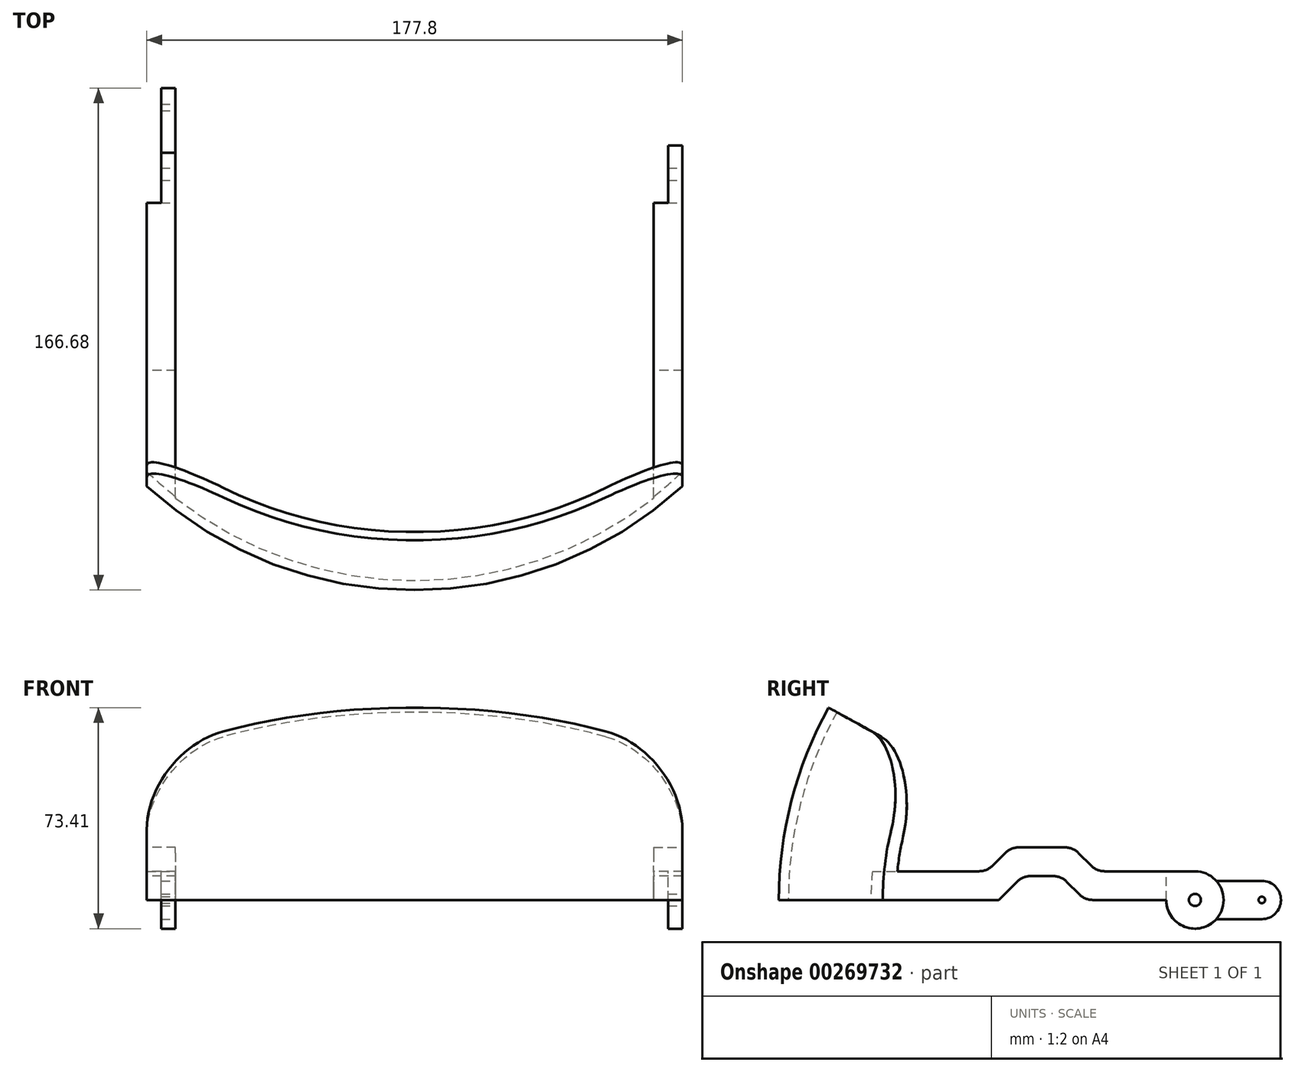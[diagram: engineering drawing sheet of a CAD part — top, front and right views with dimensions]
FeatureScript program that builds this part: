
annotation { "Feature Type Name" : "Feature", "Feature Type Description" : "" }
export const myFeature = defineFeature(function(context is Context, id is Id, definition is map)
    precondition{}
    {
        {
            var Q0;
            Q0=qCreatedBy(makeId("Right.planeOp"),FACE);
            var sketch = newSketch(context, id + "F0", { "sketchPlane" : qUnion([Q0])});
            skArc(sketch, "E0", {"start": v(0, 131.76) * mm, "mid": v(-131.76, 0) * mm, "end": v(0, -131.76) * mm});
            skArc(sketch, "E1", {"start": v(0, 128.59) * mm, "mid": v(-128.59, 0) * mm, "end": v(0, -128.59) * mm});
            skLineSegment(sketch, "E2", {"start": v(0, 131.76) * mm, "end": v(0, 128.59) * mm});
            skLineSegment(sketch, "E3.trimOffspring", {"start": v(0, 0) * mm, "end": v(0, -131.76) * mm});
            skPoint(sketch, "E4.orphan", {"position": v(0, 135.47) * mm});
            skSolve(sketch);
        }
        {
            var Q0;
            Q0=qSketchRegion(id+"F0",true);
            var Q1;
            Q1=sQuery(id+"F0.wireOp",EDGE,"E3.trimOffspring");
            revolve(context, id + "F1", {"entities" : qUnion([Q0]), "axis" : qUnion([Q1]), "revolveType" : RevolveType.FULL});
        }
        {
            var Q0;
            Q0=qCreatedBy(makeId("Front.planeOp"),FACE);
            var sketch = newSketch(context, id + "F2", { "sketchPlane" : qUnion([Q0])});
            skLineSegment(sketch, "E5.left", {"start": v(88.9, 152.6) * mm, "end": v(88.9, -152.6) * mm});
            skLineSegment(sketch, "E5.right", {"start": v(-88.9, 152.6) * mm, "end": v(-88.9, -152.6) * mm});
            skPoint(sketch, "E5.middle", {"position": v(0, 0) * mm});
            skLineSegment(sketch, "E6.bottom", {"start": v(230.94, 152.6) * mm, "end": v(88.9, 152.6) * mm});
            skLineSegment(sketch, "E6.top", {"start": v(230.94, -152.6) * mm, "end": v(88.9, -152.6) * mm});
            skLineSegment(sketch, "E6.left", {"start": v(230.94, 152.6) * mm, "end": v(230.94, -152.6) * mm});
            skLineSegment(sketch, "E6.right", {"start": v(-230.94, 152.6) * mm, "end": v(-230.94, -152.6) * mm});
            skLineSegment(sketch, "E7.trimOffspring", {"start": v(-88.9, 152.6) * mm, "end": v(-230.94, 152.6) * mm});
            skPoint(sketch, "E5.bottom.start.orphan", {"position": v(88.9, 254.33) * mm});
            skPoint(sketch, "E8.orphan", {"position": v(-88.9, 254.33) * mm});
            skLineSegment(sketch, "E9.trimOffspring", {"start": v(-88.9, -152.6) * mm, "end": v(-230.94, -152.6) * mm});
            skPoint(sketch, "E5.top.end.orphan", {"position": v(-88.9, -254.33) * mm});
            skPoint(sketch, "E5.top.start.orphan", {"position": v(88.9, -254.33) * mm});
            skSolve(sketch);
        }
        {
            var Q0;
            Q0=qSketchRegion(id+"F2",true);
            extrude(context, id + "F3", {"entities" : qUnion([Q0]), "operationType" : NewBodyOperationType.REMOVE, "endBound" : BoundingType.SYMMETRIC, "oppositeDirection" : true, "depth" : 304.8 * mm});
        }
        {
            var Q0;
            Q0=qCreatedBy(makeId("Right.planeOp"),FACE);
            var sketch = newSketch(context, id + "F4", { "sketchPlane" : qUnion([Q0])});
            skLineSegment(sketch, "E10", {"start": v(0, 0) * mm, "end": v(-147.9, 0) * mm});
            skLineSegment(sketch, "E11", {"start": v(0, 0) * mm, "end": v(-129.35, 71.7) * mm});
            skArc(sketch, "E12", {"start": v(-147.9, 0) * mm, "mid": v(143.19, -37.03) * mm, "end": v(-129.35, 71.7) * mm});
            skSolve(sketch);
        }
        {
            var Q0;
            Q0=qSketchRegion(id+"F4",true);
            extrude(context, id + "F5", {"entities" : qUnion([Q0]), "operationType" : NewBodyOperationType.REMOVE, "endBound" : BoundingType.SYMMETRIC, "depth" : 304.8 * mm});
        }
        {
            var Q0;
            Q0=makeQuery(id+"F5.boolean.opBoolean","INTERSECT",EDGE,{"derivedFrom":[makeQuery(id+"F3.boolean.opBoolean","COPY",FACE,{"derivedFrom":makeQuery(id+"F3.opExtrude","SWEPT_FACE",FACE,{"disambiguationData":[OSD([sQuery(id+"F2.wireOp",EDGE,"E5.left")])]})}),makeQuery(id+"F5.opExtrude","SWEPT_FACE",FACE,{"disambiguationData":[OSD([sQuery(id+"F4.wireOp",EDGE,"E11")])]})]});
            var Q1;
            Q1=makeQuery(id+"F5.boolean.opBoolean","INTERSECT",EDGE,{"derivedFrom":[makeQuery(id+"F3.boolean.opBoolean","COPY",FACE,{"derivedFrom":makeQuery(id+"F3.opExtrude","SWEPT_FACE",FACE,{"disambiguationData":[OSD([sQuery(id+"F2.wireOp",EDGE,"E5.right")])]})}),makeQuery(id+"F5.opExtrude","SWEPT_FACE",FACE,{"disambiguationData":[OSD([sQuery(id+"F4.wireOp",EDGE,"E11")])]})]});
            fillet(context, id + "F6", {"entities" : qUnion([Q0, Q1]), "radius" : 25.4 * mm, "tangentPropagation" : true, "allowEdgeOverflow" : false});
        }
        {
            var Q0;
            Q0=qCreatedBy(makeId("Front.planeOp"),FACE);
            var sketch = newSketch(context, id + "F7", { "sketchPlane" : qUnion([Q0])});
            skLineSegment(sketch, "E13", {"start": v(88.9, 0) * mm, "end": v(79.38, 0) * mm});
            skLineSegment(sketch, "E14", {"start": v(88.9, 0) * mm, "end": v(88.9, 9.52) * mm});
            skLineSegment(sketch, "E15", {"start": v(-88.9, 0) * mm, "end": v(-88.9, 9.52) * mm});
            skLineSegment(sketch, "E16", {"start": v(88.9, 9.52) * mm, "end": v(79.38, 9.52) * mm});
            skLineSegment(sketch, "E17", {"start": v(79.38, 9.52) * mm, "end": v(79.38, 0) * mm});
            skLineSegment(sketch, "E18", {"start": v(-79.38, 9.52) * mm, "end": v(-79.38, 0) * mm});
            skLineSegment(sketch, "E19.trimOffspring", {"start": v(-79.38, 9.52) * mm, "end": v(-88.9, 9.52) * mm});
            skLineSegment(sketch, "E20.trimOffspring", {"start": v(-79.38, 0) * mm, "end": v(-88.9, 0) * mm});
            skPoint(sketch, "E21.orphan", {"position": v(-88.9, 10) * mm});
            skPoint(sketch, "E22.orphan", {"position": v(94.46, 0) * mm});
            skSolve(sketch);
        }
        {
            var Q0;
            Q0=qSketchRegion(id+"F7",true);
            var Q1;
            Q1=makeQuery(id+"F1.opRevolve","SWEPT_FACE",FACE,{"disambiguationData":[OSD([sQuery(id+"F0.wireOp",EDGE,"E1")])]});
            extrude(context, id + "F8", {"entities" : qUnion([Q0]), "operationType" : NewBodyOperationType.ADD, "endBound" : BoundingType.UP_TO_SURFACE, "endBoundEntityFace" : qUnion([Q1]), "depth" : 25.4 * mm});
        }
        {
            var Q0;
            Q0=makeQuery(id+"F8.opExtrude","CAP_FACE",FACE,{"disambiguationData":[OSD([sQuery(id+"F7.wireOp",EDGE,"E13"),sQuery(id+"F7.wireOp",EDGE,"E14"),sQuery(id+"F7.wireOp",EDGE,"E16"),sQuery(id+"F7.wireOp",EDGE,"E17")])],"isStart":true});
            var sketch = newSketch(context, id + "F9", { "sketchPlane" : qUnion([Q0])});
            skLineSegment(sketch, "E23.bottom", {"start": v(-88.9, 9.52) * mm, "end": v(-79.38, 9.52) * mm});
            skLineSegment(sketch, "E23.top", {"start": v(-88.9, 0) * mm, "end": v(-79.38, 0) * mm});
            skLineSegment(sketch, "E23.left", {"start": v(-88.9, 9.52) * mm, "end": v(-88.9, 0) * mm});
            skLineSegment(sketch, "E23.right", {"start": v(-79.38, 9.52) * mm, "end": v(-79.38, 0) * mm});
            skSolve(sketch);
        }
        {
            var Q0;
            Q0=makeQuery(id+"F8.opExtrude","CAP_FACE",FACE,{"disambiguationData":[OSD([sQuery(id+"F7.wireOp",EDGE,"E15"),sQuery(id+"F7.wireOp",EDGE,"E18"),sQuery(id+"F7.wireOp",EDGE,"E19.trimOffspring"),sQuery(id+"F7.wireOp",EDGE,"E20.trimOffspring")])],"isStart":true});
            var sketch = newSketch(context, id + "F10", { "sketchPlane" : qUnion([Q0])});
            skLineSegment(sketch, "E24.bottom", {"start": v(79.38, 9.52) * mm, "end": v(88.9, 9.52) * mm});
            skLineSegment(sketch, "E24.top", {"start": v(79.38, 0) * mm, "end": v(88.9, 0) * mm});
            skLineSegment(sketch, "E24.left", {"start": v(79.38, 9.52) * mm, "end": v(79.38, 0) * mm});
            skLineSegment(sketch, "E24.right", {"start": v(88.9, 9.52) * mm, "end": v(88.9, 0) * mm});
            skSolve(sketch);
        }
        {
            var Q0;
            Q0 = qSketchRegion(id + "F9", true);
            var Q1;
            Q1 = qSketchRegion(id + "F10", true);
            extrude(context, id + "F11", {"entities" : qUnion([Q0, Q1]), "operationType" : NewBodyOperationType.ADD, "depth" : 6.35 * mm, "offsetDistance" : 25.4 * mm});
        }
        {
            var Q0;
            Q0=makeQuery(id+"F8.boolean.opBoolean","MERGE",FACE,{"derivedFrom":[makeQuery(id+"F3.boolean.opBoolean","COPY",FACE,{"derivedFrom":makeQuery(id+"F3.opExtrude","SWEPT_FACE",FACE,{"disambiguationData":[OSD([sQuery(id+"F2.wireOp",EDGE,"E5.left")])]})}),makeQuery(id+"F8.opExtrude","SWEPT_FACE",FACE,{"disambiguationData":[OSD([sQuery(id+"F7.wireOp",EDGE,"E14")])]})]});
            var sketch = newSketch(context, id + "F12", { "sketchPlane" : qUnion([Q0])});
            skLineSegment(sketch, "E25", {"start": v(-16.7, 0) * mm, "end": v(-30.16, 0) * mm});
            skPoint(sketch, "E26.endSnap0", {"position": v(6.35, 4.76) * mm});
            skLineSegment(sketch, "E27", {"start": v(-34.15, 17.46) * mm, "end": v(-54.75, 17.46) * mm});
            skLineSegment(sketch, "E28", {"start": v(-34.93, 17.46) * mm, "end": v(-34.93, 4.76) * mm});
            skLineSegment(sketch, "E29", {"start": v(-53.98, 17.46) * mm, "end": v(-53.98, 4.76) * mm});
            skLineSegment(sketch, "E30", {"start": v(-64.27, 7.94) * mm, "end": v(-24.63, 7.94) * mm});
            skPoint(sketch, "E31.orphan", {"position": v(-81.5, 4.76) * mm});
            skLineSegment(sketch, "E32", {"start": v(-53.98, 4.76) * mm, "end": v(-50.8, 7.94) * mm});
            skLineSegment(sketch, "E33", {"start": v(-34.93, 4.76) * mm, "end": v(-38.1, 7.94) * mm});
            skLineSegment(sketch, "E34", {"start": v(-53.98, 4.76) * mm, "end": v(-58.74, 0) * mm});
            skLineSegment(sketch, "E35", {"start": v(-34.93, 4.76) * mm, "end": v(-30.16, 0) * mm});
            skPoint(sketch, "E36.start.orphan", {"position": v(6.35, 19.8) * mm});
            skLineSegment(sketch, "E37", {"start": v(-54.75, 17.46) * mm, "end": v(-72.2, 0) * mm});
            skLineSegment(sketch, "E38", {"start": v(-34.15, 17.46) * mm, "end": v(-16.7, 0) * mm});
            skPoint(sketch, "E39.orphan", {"position": v(6.35, 17.46) * mm});
            skLineSegment(sketch, "E40.trimOffspring", {"start": v(-58.74, 0) * mm, "end": v(-72.2, 0) * mm});
            skSolve(sketch);
        }
        {
            var Q0;
            Q0=qSketchRegion(id+"F12",true);
            extrude(context, id + "F13", {"entities" : qUnion([Q0]), "operationType" : NewBodyOperationType.ADD, "oppositeDirection" : true, "depth" : 9.52 * mm});
        }
        {
            var Q0;
            Q0=makeQuery(id+"F8.boolean.opBoolean","MERGE",FACE,{"derivedFrom":[makeQuery(id+"F3.boolean.opBoolean","COPY",FACE,{"derivedFrom":makeQuery(id+"F3.opExtrude","SWEPT_FACE",FACE,{"disambiguationData":[OSD([sQuery(id+"F2.wireOp",EDGE,"E5.right")])]})}),makeQuery(id+"F8.opExtrude","SWEPT_FACE",FACE,{"disambiguationData":[OSD([sQuery(id+"F7.wireOp",EDGE,"E15")])]})]});
            var sketch = newSketch(context, id + "F14", { "sketchPlane" : qUnion([Q0])});
            skLineSegment(sketch, "E41", {"start": v(34.15, 17.46) * mm, "end": v(54.75, 17.46) * mm});
            skLineSegment(sketch, "E42", {"start": v(34.93, 7.94) * mm, "end": v(34.93, 0) * mm});
            skLineSegment(sketch, "E43", {"start": v(53.98, 7.94) * mm, "end": v(53.98, 0) * mm});
            skLineSegment(sketch, "E44", {"start": v(34.93, 0) * mm, "end": v(53.98, 0) * mm});
            skLineSegment(sketch, "E45", {"start": v(34.93, 4.76) * mm, "end": v(38.1, 7.94) * mm});
            skLineSegment(sketch, "E46", {"start": v(53.98, 4.76) * mm, "end": v(49.21, 9.53) * mm});
            skLineSegment(sketch, "E47", {"start": v(24.63, 7.94) * mm, "end": v(34.93, 7.94) * mm});
            skLineSegment(sketch, "E48", {"start": v(34.15, 17.46) * mm, "end": v(24.63, 7.94) * mm});
            skLineSegment(sketch, "E49", {"start": v(54.75, 17.46) * mm, "end": v(64.27, 7.94) * mm});
            skPoint(sketch, "E50.orphan", {"position": v(34.93, 9.52) * mm});
            skLineSegment(sketch, "E51.trimOffspring", {"start": v(53.98, 7.94) * mm, "end": v(64.27, 7.94) * mm});
            skPoint(sketch, "E52.orphan", {"position": v(53.98, 9.52) * mm});
            skSolve(sketch);
        }
        {
            var Q0;
            Q0=qSketchRegion(id+"F14",true);
            extrude(context, id + "F15", {"entities" : qUnion([Q0]), "operationType" : NewBodyOperationType.ADD, "oppositeDirection" : true, "depth" : 9.52 * mm});
        }
        {
            var Q0;
            Q0=qCreatedBy(makeId("Right.planeOp"),FACE);
            var sketch = newSketch(context, id + "F16", { "sketchPlane" : qUnion([Q0])});
            skLineSegment(sketch, "E53", {"start": v(-30.16, 0) * mm, "end": v(-58.74, 0) * mm});
            skLineSegment(sketch, "E54", {"start": v(-38.1, 7.94) * mm, "end": v(-50.8, 7.94) * mm});
            skLineSegment(sketch, "E55", {"start": v(-53.98, 7.94) * mm, "end": v(-53.98, 4.76) * mm});
            skLineSegment(sketch, "E56.trimOffspring", {"start": v(-34.93, 4.76) * mm, "end": v(-34.93, 7.94) * mm});
            skLineSegment(sketch, "E57", {"start": v(-53.98, 4.76) * mm, "end": v(-50.8, 7.94) * mm});
            skLineSegment(sketch, "E58", {"start": v(-34.93, 4.76) * mm, "end": v(-38.1, 7.94) * mm});
            skLineSegment(sketch, "E59", {"start": v(-53.98, 4.76) * mm, "end": v(-58.74, 0) * mm});
            skLineSegment(sketch, "E60", {"start": v(-34.93, 4.76) * mm, "end": v(-30.16, 0) * mm});
            skSolve(sketch);
        }
        {
            var Q0;
            Q0=qSketchRegion(id+"F16",true);
            extrude(context, id + "F17", {"entities" : qUnion([Q0]), "operationType" : NewBodyOperationType.REMOVE, "endBound" : BoundingType.SYMMETRIC, "depth" : 177.8 * mm});
        }
        {
            var Q0;
            Q0=makeQuery(id+"F9Fqv3LpDGS5zFg_1.boolean.opBoolean","MERGE",FACE,{"derivedFrom":[makeQuery(id+"F8.boolean.opBoolean","MERGE",FACE,{"derivedFrom":[makeQuery(id+"F3.boolean.opBoolean","COPY",FACE,{"derivedFrom":makeQuery(id+"F3.opExtrude","SWEPT_FACE",FACE,{"disambiguationData":[OSD([sQuery(id+"F2.wireOp",EDGE,"E5.left")])]})}),makeQuery(id+"F8.opExtrude","SWEPT_FACE",FACE,{"disambiguationData":[OSD([sQuery(id+"F7.wireOp",EDGE,"E14")])]})]}),makeQuery(id+"F9Fqv3LpDGS5zFg_1.opExtrude","CAP_FACE",FACE,{"disambiguationData":[OSD([sQuery(id+"Fdyxyt73cwK6mQ5_1.wireOp",EDGE,"uge7HxcK-xsYJ-EXUT-pD71-h3y1mwA4NyrV"),sQuery(id+"Fdyxyt73cwK6mQ5_1.wireOp",EDGE,"hfxr85zl-CjJz-dNnQ-cUyG-KzP6Vcheir9o"),sQuery(id+"Fdyxyt73cwK6mQ5_1.wireOp",EDGE,"DYdveK2D-yC2o-hGCK-GH33-UXKGGb30pmTF"),sQuery(id+"Fdyxyt73cwK6mQ5_1.wireOp",EDGE,"KyHsQCAR-jBkV-1PyX-yX3m-mguW6c5BXjM3"),sQuery(id+"Fdyxyt73cwK6mQ5_1.wireOp",EDGE,"KXiKUkZQ-NJSx-R7BF-pjD5-MABOeaKY5b3t"),sQuery(id+"Fdyxyt73cwK6mQ5_1.wireOp",EDGE,"uAoFoTMZ-oCW3-4zug-ka1U-f82iXX2Ucrwf"),sQuery(id+"Fdyxyt73cwK6mQ5_1.wireOp",EDGE,"oFfLLbmo-RIOd-E5QO-eRZp-mn8jqRh1hiLr"),sQuery(id+"Fdyxyt73cwK6mQ5_1.wireOp",EDGE,"XboE2R6W-MqqC-2Aew-ZZfI-9xdbT96ioL7k"),sQuery(id+"Fdyxyt73cwK6mQ5_1.wireOp",EDGE,"il7hj7Cw-iAn3-ZAEo-7ila-wyK5fjaZt0oG"),sQuery(id+"Fdyxyt73cwK6mQ5_1.wireOp",EDGE,"2c3155a9-a74c-4d56-af0e-1345a1cb9d5a.trimOffspring")])],"isStart":true})]});
            var sketch = newSketch(context, id + "F18", { "sketchPlane" : qUnion([Q0])});
            skCircle(sketch, "E61", {"center": v(6.35, 0) * mm, "radius": 9.52 * mm});
            skSolve(sketch);
        }
        {
            var Q0;
            Q0=qSketchRegion(id+"F18",true);
            extrude(context, id + "F19", {"entities" : qUnion([Q0]), "operationType" : NewBodyOperationType.ADD, "oppositeDirection" : true, "depth" : 4.76 * mm});
        }
        {
            var Q0;
            Q0=makeQuery(id+"F15.boolean.opBoolean","MERGE",FACE,{"derivedFrom":[makeQuery(id+"F8.opExtrude","SWEPT_FACE",FACE,{"disambiguationData":[OSD([sQuery(id+"F7.wireOp",EDGE,"E18")])]}),makeQuery(id+"F15.opExtrude","CAP_FACE",FACE,{"disambiguationData":[OSD([sQuery(id+"F14.wireOp",EDGE,"E41"),sQuery(id+"F14.wireOp",EDGE,"E42"),sQuery(id+"F14.wireOp",EDGE,"E43"),sQuery(id+"F14.wireOp",EDGE,"E44"),sQuery(id+"F14.wireOp",EDGE,"E47"),sQuery(id+"F14.wireOp",EDGE,"E48"),sQuery(id+"F14.wireOp",EDGE,"E49"),sQuery(id+"F14.wireOp",EDGE,"E51.trimOffspring")])],"isStart":false})]});
            var sketch = newSketch(context, id + "F20", { "sketchPlane" : qUnion([Q0])});
            skCircle(sketch, "E62", {"center": v(6.35, 0) * mm, "radius": 9.52 * mm});
            skSolve(sketch);
        }
        {
            var Q0;
            Q0=qSketchRegion(id+"F20",true);
            extrude(context, id + "F21", {"entities" : qUnion([Q0]), "operationType" : NewBodyOperationType.ADD, "oppositeDirection" : true, "depth" : 4.76 * mm});
        }
        {
            var Q0;
            Q0=qCreatedBy(makeId("Right.planeOp"),FACE);
            var sketch = newSketch(context, id + "F22", { "sketchPlane" : qUnion([Q0])});
            skCircle(sketch, "E63", {"center": v(6.35, 0) * mm, "radius": 2 * mm});
            skSolve(sketch);
        }
        {
            var Q0;
            Q0=qSketchRegion(id+"F22",true);
            extrude(context, id + "F23", {"entities" : qUnion([Q0]), "operationType" : NewBodyOperationType.REMOVE, "endBound" : BoundingType.SYMMETRIC, "oppositeDirection" : true, "depth" : 177.8 * mm});
        }
        {
            var Q0;
            Q0=makeQuery(id+"F15.boolean.opBoolean","MERGE",FACE,{"derivedFrom":[makeQuery(id+"F8.boolean.opBoolean","MERGE",FACE,{"derivedFrom":[makeQuery(id+"F3.boolean.opBoolean","COPY",FACE,{"derivedFrom":makeQuery(id+"F3.opExtrude","SWEPT_FACE",FACE,{"disambiguationData":[OSD([sQuery(id+"F2.wireOp",EDGE,"E5.right")])]})}),makeQuery(id+"F8.opExtrude","SWEPT_FACE",FACE,{"disambiguationData":[OSD([sQuery(id+"F7.wireOp",EDGE,"E15")])]})]}),makeQuery(id+"F15.opExtrude","CAP_FACE",FACE,{"disambiguationData":[OSD([sQuery(id+"F14.wireOp",EDGE,"E41"),sQuery(id+"F14.wireOp",EDGE,"E42"),sQuery(id+"F14.wireOp",EDGE,"E43"),sQuery(id+"F14.wireOp",EDGE,"E44"),sQuery(id+"F14.wireOp",EDGE,"E47"),sQuery(id+"F14.wireOp",EDGE,"E48"),sQuery(id+"F14.wireOp",EDGE,"E49"),sQuery(id+"F14.wireOp",EDGE,"E51.trimOffspring")])],"isStart":true})]});
            var sketch = newSketch(context, id + "F24", { "sketchPlane" : qUnion([Q0])});
            skArc(sketch, "E64", {"start": v(-6.35, 9.52) * mm, "mid": v(-13.09, -6.74) * mm, "end": v(3.17, 0) * mm});
            skLineSegment(sketch, "E65", {"start": v(3.17, 0) * mm, "end": v(3.17, 9.52) * mm});
            skLineSegment(sketch, "E66", {"start": v(3.17, 9.52) * mm, "end": v(-6.35, 9.52) * mm});
            skSolve(sketch);
        }
        {
            var Q0;
            Q0=qSketchRegion(id+"F24",true);
            extrude(context, id + "F25", {"entities" : qUnion([Q0]), "operationType" : NewBodyOperationType.REMOVE, "oppositeDirection" : true, "depth" : 4.76 * mm});
        }
        {
            var Q0;
            Q0=makeQuery(id+"F9Fqv3LpDGS5zFg_1.boolean.opBoolean","MERGE",FACE,{"derivedFrom":[makeQuery(id+"F8.opExtrude","SWEPT_FACE",FACE,{"disambiguationData":[OSD([sQuery(id+"F7.wireOp",EDGE,"E17")])]}),makeQuery(id+"F9Fqv3LpDGS5zFg_1.opExtrude","CAP_FACE",FACE,{"disambiguationData":[OSD([sQuery(id+"Fdyxyt73cwK6mQ5_1.wireOp",EDGE,"uge7HxcK-xsYJ-EXUT-pD71-h3y1mwA4NyrV"),sQuery(id+"Fdyxyt73cwK6mQ5_1.wireOp",EDGE,"hfxr85zl-CjJz-dNnQ-cUyG-KzP6Vcheir9o"),sQuery(id+"Fdyxyt73cwK6mQ5_1.wireOp",EDGE,"DYdveK2D-yC2o-hGCK-GH33-UXKGGb30pmTF"),sQuery(id+"Fdyxyt73cwK6mQ5_1.wireOp",EDGE,"KyHsQCAR-jBkV-1PyX-yX3m-mguW6c5BXjM3"),sQuery(id+"Fdyxyt73cwK6mQ5_1.wireOp",EDGE,"KXiKUkZQ-NJSx-R7BF-pjD5-MABOeaKY5b3t"),sQuery(id+"Fdyxyt73cwK6mQ5_1.wireOp",EDGE,"uAoFoTMZ-oCW3-4zug-ka1U-f82iXX2Ucrwf"),sQuery(id+"Fdyxyt73cwK6mQ5_1.wireOp",EDGE,"oFfLLbmo-RIOd-E5QO-eRZp-mn8jqRh1hiLr"),sQuery(id+"Fdyxyt73cwK6mQ5_1.wireOp",EDGE,"XboE2R6W-MqqC-2Aew-ZZfI-9xdbT96ioL7k"),sQuery(id+"Fdyxyt73cwK6mQ5_1.wireOp",EDGE,"il7hj7Cw-iAn3-ZAEo-7ila-wyK5fjaZt0oG"),sQuery(id+"Fdyxyt73cwK6mQ5_1.wireOp",EDGE,"2c3155a9-a74c-4d56-af0e-1345a1cb9d5a.trimOffspring")])],"isStart":false})]});
            var sketch = newSketch(context, id + "F26", { "sketchPlane" : qUnion([Q0])});
            skArc(sketch, "E67", {"start": v(-6.35, 9.52) * mm, "mid": v(-13.09, -6.74) * mm, "end": v(3.17, 0) * mm});
            skLineSegment(sketch, "E68", {"start": v(3.17, 0) * mm, "end": v(3.17, 9.52) * mm});
            skLineSegment(sketch, "E69", {"start": v(3.17, 9.52) * mm, "end": v(-6.35, 9.52) * mm});
            skSolve(sketch);
        }
        {
            var Q0;
            Q0=qSketchRegion(id+"F26",true);
            extrude(context, id + "F27", {"entities" : qUnion([Q0]), "operationType" : NewBodyOperationType.REMOVE, "oppositeDirection" : true, "depth" : 4.76 * mm});
        }
        {
            var Q0;
            Q0=makeQuery(id+"F8.opExtrude","TWEAK_EDGE",EDGE,{"derivedFrom":[makeQuery(id+"F1.opRevolve","SWEPT_FACE",FACE,{"disambiguationData":[OSD([sQuery(id+"F0.wireOp",EDGE,"E1")])]}),makeQuery(id+"F7.imprint","IMPRINT",EDGE,{"derivedFrom":sQuery(id+"F7.wireOp",EDGE,"E19.trimOffspring")})]});
            var Q1;
            Q1=makeQuery(id+"F8.opExtrude","TWEAK_EDGE",EDGE,{"derivedFrom":[makeQuery(id+"F1.opRevolve","SWEPT_FACE",FACE,{"disambiguationData":[OSD([sQuery(id+"F0.wireOp",EDGE,"E1")])]}),makeQuery(id+"F7.imprint","IMPRINT",EDGE,{"derivedFrom":sQuery(id+"F7.wireOp",EDGE,"E16")})]});
            var Q2;
            Q2=makeQuery(id+"F27.boolean.opBoolean","COPY",EDGE,{"derivedFrom":makeQuery(id+"F27.opExtrude","CAP_EDGE",EDGE,{"disambiguationData":[OSD([sQuery(id+"F26.wireOp",EDGE,"E68")])],"isStart":true})});
            var Q3;
            Q3=makeQuery(id+"F13.boolean.opBoolean","INTERSECT",EDGE,{"derivedFrom":[makeQuery(id+"F8.opExtrude","SWEPT_FACE",FACE,{"disambiguationData":[OSD([sQuery(id+"F7.wireOp",EDGE,"E16")])]}),makeQuery(id+"F13.opExtrude","SWEPT_FACE",FACE,{"disambiguationData":[OSD([sQuery(id+"F12.wireOp",EDGE,"E38")])]})]});
            var Q4;
            Q4=makeQuery(id+"F13.opExtrude","SWEPT_EDGE",EDGE,{"disambiguationData":[OSD([sQuery(id+"F12.wireOp",EDGE,"E27"),sQuery(id+"F12.wireOp",EDGE,"E38")])]});
            var Q5;
            Q5=makeQuery(id+"F13.opExtrude","SWEPT_EDGE",EDGE,{"disambiguationData":[OSD([sQuery(id+"F12.wireOp",EDGE,"E27"),sQuery(id+"F12.wireOp",EDGE,"E37")])]});
            var Q6;
            Q6=makeQuery(id+"F13.boolean.opBoolean","INTERSECT",EDGE,{"derivedFrom":[makeQuery(id+"F8.opExtrude","SWEPT_FACE",FACE,{"disambiguationData":[OSD([sQuery(id+"F7.wireOp",EDGE,"E16")])]}),makeQuery(id+"F13.opExtrude","SWEPT_FACE",FACE,{"disambiguationData":[OSD([sQuery(id+"F12.wireOp",EDGE,"E37")])]})]});
            var Q7;
            Q7=makeQuery(id+"F15.boolean.opBoolean","INTERSECT",EDGE,{"derivedFrom":[makeQuery(id+"F8.opExtrude","SWEPT_FACE",FACE,{"disambiguationData":[OSD([sQuery(id+"F7.wireOp",EDGE,"E19.trimOffspring")])]}),makeQuery(id+"F15.opExtrude","SWEPT_FACE",FACE,{"disambiguationData":[OSD([sQuery(id+"F14.wireOp",EDGE,"E48")])]})]});
            var Q8;
            Q8=makeQuery(id+"F15.opExtrude","SWEPT_EDGE",EDGE,{"disambiguationData":[OSD([sQuery(id+"F14.wireOp",EDGE,"E41"),sQuery(id+"F14.wireOp",EDGE,"E48")])]});
            var Q9;
            Q9=makeQuery(id+"F15.opExtrude","SWEPT_EDGE",EDGE,{"disambiguationData":[OSD([sQuery(id+"F14.wireOp",EDGE,"E41"),sQuery(id+"F14.wireOp",EDGE,"E49")])]});
            var Q10;
            Q10=makeQuery(id+"F15.boolean.opBoolean","INTERSECT",EDGE,{"derivedFrom":[makeQuery(id+"F8.opExtrude","SWEPT_FACE",FACE,{"disambiguationData":[OSD([sQuery(id+"F7.wireOp",EDGE,"E19.trimOffspring")])]}),makeQuery(id+"F15.opExtrude","SWEPT_FACE",FACE,{"disambiguationData":[OSD([sQuery(id+"F14.wireOp",EDGE,"E49")])]})]});
            var Q11;
            {var subQ10=sQuery(id+"F16.wireOp",EDGE,"E60");Q11=makeQuery(id+"F17.boolean.opBoolean","COPY",EDGE,{"disambiguationData":[TD([makeQuery(id+"F3.boolean.opBoolean","COPY",FACE,{"derivedFrom":makeQuery(id+"F3.opExtrude","SWEPT_FACE",FACE,{"disambiguationData":[OSD([sQuery(id+"F2.wireOp",EDGE,"E5.left")])]})})])],"derivedFrom":makeQuery(id+"F17.opExtrude","SWEPT_EDGE",EDGE,{"disambiguationData":[OSD([sQuery(id+"F16.wireOp",EDGE,"E53"),subQ10])]})});}
            var Q12;
            {var subQ10=sQuery(id+"F16.wireOp",EDGE,"E59");Q12=makeQuery(id+"F17.boolean.opBoolean","COPY",EDGE,{"disambiguationData":[TD([makeQuery(id+"F3.boolean.opBoolean","COPY",FACE,{"derivedFrom":makeQuery(id+"F3.opExtrude","SWEPT_FACE",FACE,{"disambiguationData":[OSD([sQuery(id+"F2.wireOp",EDGE,"E5.left")])]})})])],"derivedFrom":makeQuery(id+"F17.opExtrude","SWEPT_EDGE",EDGE,{"disambiguationData":[OSD([sQuery(id+"F16.wireOp",EDGE,"E53"),subQ10])]})});}
            var Q13;
            {var subQ10=sQuery(id+"F16.wireOp",EDGE,"E54");var subQ11=sQuery(id+"F16.wireOp",EDGE,"E57");Q13=makeQuery(id+"F17.boolean.opBoolean","COPY",EDGE,{"disambiguationData":[TD([makeQuery(id+"F3.boolean.opBoolean","COPY",FACE,{"derivedFrom":makeQuery(id+"F3.opExtrude","SWEPT_FACE",FACE,{"disambiguationData":[OSD([sQuery(id+"F2.wireOp",EDGE,"E5.left")])]})})])],"derivedFrom":makeQuery(id+"F17.opExtrude","SWEPT_EDGE",EDGE,{"disambiguationData":[OSD([subQ10,subQ11])]})});}
            var Q14;
            {var subQ10=sQuery(id+"F16.wireOp",EDGE,"E58");var subQ11=sQuery(id+"F16.wireOp",EDGE,"E54");Q14=makeQuery(id+"F17.boolean.opBoolean","COPY",EDGE,{"disambiguationData":[TD([makeQuery(id+"F3.boolean.opBoolean","COPY",FACE,{"derivedFrom":makeQuery(id+"F3.opExtrude","SWEPT_FACE",FACE,{"disambiguationData":[OSD([sQuery(id+"F2.wireOp",EDGE,"E5.left")])]})})])],"derivedFrom":makeQuery(id+"F17.opExtrude","SWEPT_EDGE",EDGE,{"disambiguationData":[OSD([subQ11,subQ10])]})});}
            var Q15;
            {var subQ8=sQuery(id+"F16.wireOp",EDGE,"E59");Q15=makeQuery(id+"F17.boolean.opBoolean","COPY",EDGE,{"disambiguationData":[TD([makeQuery(id+"F3.boolean.opBoolean","COPY",FACE,{"derivedFrom":makeQuery(id+"F3.opExtrude","SWEPT_FACE",FACE,{"disambiguationData":[OSD([sQuery(id+"F2.wireOp",EDGE,"E5.right")])]})})])],"derivedFrom":makeQuery(id+"F17.opExtrude","SWEPT_EDGE",EDGE,{"disambiguationData":[OSD([sQuery(id+"F16.wireOp",EDGE,"E53"),subQ8])]})});}
            var Q16;
            {var subQ8=sQuery(id+"F16.wireOp",EDGE,"E54");var subQ9=sQuery(id+"F16.wireOp",EDGE,"E57");Q16=makeQuery(id+"F17.boolean.opBoolean","COPY",EDGE,{"disambiguationData":[TD([makeQuery(id+"F3.boolean.opBoolean","COPY",FACE,{"derivedFrom":makeQuery(id+"F3.opExtrude","SWEPT_FACE",FACE,{"disambiguationData":[OSD([sQuery(id+"F2.wireOp",EDGE,"E5.right")])]})})])],"derivedFrom":makeQuery(id+"F17.opExtrude","SWEPT_EDGE",EDGE,{"disambiguationData":[OSD([subQ8,subQ9])]})});}
            var Q17;
            {var subQ8=sQuery(id+"F16.wireOp",EDGE,"E54");var subQ9=sQuery(id+"F16.wireOp",EDGE,"E58");Q17=makeQuery(id+"F17.boolean.opBoolean","COPY",EDGE,{"disambiguationData":[TD([makeQuery(id+"F3.boolean.opBoolean","COPY",FACE,{"derivedFrom":makeQuery(id+"F3.opExtrude","SWEPT_FACE",FACE,{"disambiguationData":[OSD([sQuery(id+"F2.wireOp",EDGE,"E5.right")])]})})])],"derivedFrom":makeQuery(id+"F17.opExtrude","SWEPT_EDGE",EDGE,{"disambiguationData":[OSD([subQ8,subQ9])]})});}
            var Q18;
            {var subQ0=sQuery(id+"F16.wireOp",EDGE,"E60");Q18=makeQuery(id+"F17.boolean.opBoolean","COPY",EDGE,{"disambiguationData":[TD([makeQuery(id+"F3.boolean.opBoolean","COPY",FACE,{"derivedFrom":makeQuery(id+"F3.opExtrude","SWEPT_FACE",FACE,{"disambiguationData":[OSD([sQuery(id+"F2.wireOp",EDGE,"E5.right")])]})})])],"derivedFrom":makeQuery(id+"F17.opExtrude","SWEPT_EDGE",EDGE,{"disambiguationData":[OSD([sQuery(id+"F16.wireOp",EDGE,"E53"),subQ0])]})});}
            var Q19;
            Q19=makeQuery(id+"F25.boolean.opBoolean","COPY",EDGE,{"derivedFrom":makeQuery(id+"F25.opExtrude","CAP_EDGE",EDGE,{"disambiguationData":[OSD([sQuery(id+"F24.wireOp",EDGE,"E65")])],"isStart":true})});
            fillet(context, id + "F28", {"entities" : qUnion([Q0, Q1, Q2, Q3, Q4, Q5, Q6, Q7, Q8, Q9, Q10, Q11, Q12, Q13, Q14, Q15, Q16, Q17, Q18, Q19]), "radius" : 6.35 * mm, "tangentPropagation" : true, "allowEdgeOverflow" : false});
        }
        {
            var Q0;
            Q0=makeQuery(id+"F21.boolean.opBoolean","MERGE",FACE,{"derivedFrom":[makeQuery(id+"F15.boolean.opBoolean","MERGE",FACE,{"derivedFrom":[makeQuery(id+"F8.opExtrude","SWEPT_FACE",FACE,{"disambiguationData":[OSD([sQuery(id+"F7.wireOp",EDGE,"E18")])]}),makeQuery(id+"F15.opExtrude","CAP_FACE",FACE,{"disambiguationData":[OSD([sQuery(id+"F14.wireOp",EDGE,"E41"),sQuery(id+"F14.wireOp",EDGE,"E42"),sQuery(id+"F14.wireOp",EDGE,"E43"),sQuery(id+"F14.wireOp",EDGE,"E44"),sQuery(id+"F14.wireOp",EDGE,"E47"),sQuery(id+"F14.wireOp",EDGE,"E48"),sQuery(id+"F14.wireOp",EDGE,"E49"),sQuery(id+"F14.wireOp",EDGE,"E51.trimOffspring")])],"isStart":false})]}),makeQuery(id+"F21.opExtrude","CAP_FACE",FACE,{"disambiguationData":[OSD([sQuery(id+"F20.wireOp",EDGE,"E62")])],"isStart":true})]});
            var sketch = newSketch(context, id + "F29", { "sketchPlane" : qUnion([Q0])});
            skArc(sketch, "E70", {"start": v(6.35, -2) * mm, "mid": v(8.35, 0) * mm, "end": v(6.35, 2) * mm});
            skLineSegment(sketch, "E71.bottom", {"start": v(28.57, 6.35) * mm, "end": v(6.35, 6.35) * mm});
            skLineSegment(sketch, "E71.top", {"start": v(28.58, -6.35) * mm, "end": v(6.35, -6.35) * mm});
            skLineSegment(sketch, "E72", {"start": v(6.35, 6.35) * mm, "end": v(6.35, 2) * mm});
            skPoint(sketch, "E73", {"position": v(28.57, 0) * mm});
            skArc(sketch, "E74", {"start": v(28.58, -6.35) * mm, "mid": v(34.93, 0) * mm, "end": v(28.57, 6.35) * mm});
            skPoint(sketch, "E71.right.end.orphan", {"position": v(-50.8, -6.35) * mm});
            skPoint(sketch, "E71.right.start.orphan", {"position": v(6.35, 6.35) * mm});
            skLineSegment(sketch, "E75.trimOffspring", {"start": v(6.35, -2) * mm, "end": v(6.35, -6.35) * mm});
            skPoint(sketch, "E76.orphan", {"position": v(0, 11.57) * mm});
            skPoint(sketch, "E77.orphan", {"position": v(50.8, 6.35) * mm});
            skPoint(sketch, "E78.orphan", {"position": v(6.35, -6.35) * mm});
            skPoint(sketch, "E79.orphan", {"position": v(31.75, 0) * mm});
            skCircle(sketch, "E80", {"center": v(28.57, 0) * mm, "radius": 1.08 * mm});
            skSolve(sketch);
        }
        {
            var Q0;
            Q0=qSketchRegion(id+"F29",true);
            extrude(context, id + "F30", {"entities" : qUnion([Q0]), "operationType" : NewBodyOperationType.ADD, "oppositeDirection" : true, "depth" : 4.76 * mm});
        }
    });
